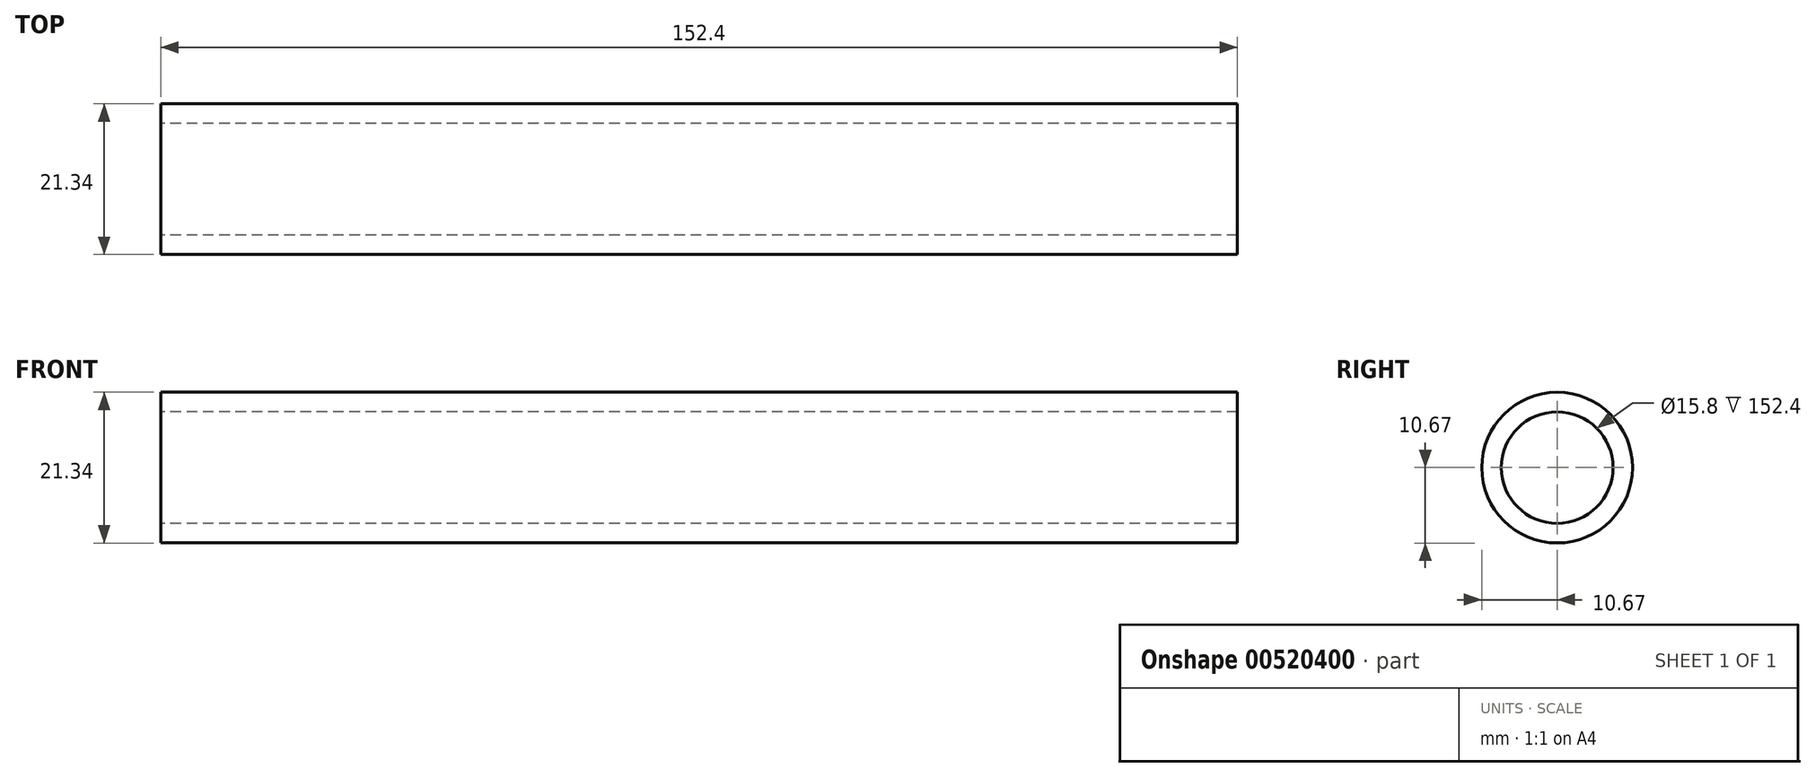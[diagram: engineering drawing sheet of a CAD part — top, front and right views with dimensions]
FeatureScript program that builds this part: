
annotation { "Feature Type Name" : "Feature", "Feature Type Description" : "" }
export const myFeature = defineFeature(function(context is Context, id is Id, definition is map)
    precondition{}
    {
        {
            var Q0;
            Q0=qCreatedBy(makeId("Right.planeOp"),FACE);
            var sketch = newSketch(context, id + "F0", { "sketchPlane" : qUnion([Q0])});
            skCircle(sketch, "E0", {"center": v(0, 0) * mm, "radius": 7.9 * mm});
            skCircle(sketch, "E1", {"center": v(0, 0) * mm, "radius": 10.67 * mm});
            skSolve(sketch);
        }
        {
            var Q0;
            Q0=makeQuery(id+"F0.imprint","IMPRINT",FACE,{"disambiguationData":[TD([[makeQuery(id+"F0.imprint","IMPRINT",EDGE,{"derivedFrom":sQuery(id+"F0.wireOp",EDGE,"E0")}),-1.0]])]});
            extrude(context, id + "F1", {"entities" : qUnion([Q0]), "depth" : 152.4 * mm, "offsetDistance" : 25.4 * mm});
        }
    });
